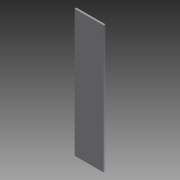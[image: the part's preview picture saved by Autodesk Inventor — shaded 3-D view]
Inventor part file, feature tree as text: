
AUTODESK INVENTOR PART (.ipt)
format: ipt  version: 2011 (Build 150239000, 239)  size: 125,440 bytes
history: native  units: in
note: dims shown in document units (in); Inventor stores cm internally (conversion verified against a paired STEP export)
features: extrude x9, sketch x9
ambient origin geometry x8: Origin, YZ Plane, XZ Plane, XY Plane, X Axis, Y Axis, Z Axis, Center Point
bodies: Solid1 (feature_tree)
feature tree (18):
  extrude  "Extrusion1"  Depth=12.0in
  extrude  "Extrusion2"  Depth=0.5in TaperAngle=0.0deg
  extrude  "Extrusion3"  Depth=1.5in TaperAngle=0.0deg
  extrude  "Extrusion4"  Depth=0.25in TaperAngle=0.0deg
  extrude  "Extrusion5"  Depth=0.5in TaperAngle=0.0deg
  extrude  "Extrusion6"  Depth=1.0in TaperAngle=0.0deg
  extrude  "Extrusion7"  Depth=1.0in TaperAngle=0.0deg
  extrude  "Extrusion8"  [1 undecoded]
  extrude  "Extrusion9"  [1 undecoded]
  sketch  "Sketch1"  dims[d0=5.5in d1=12.0in]
  sketch  "Sketch2"  dims[d2=0.25in d3=0.0in d4=0.5in d5=0.0in]
  sketch  "Sketch3"  dims[d6=0.5in d7=0.0in d8=1.5in d9=0.0in]
  sketch  "Sketch4"  dims[d10=10.0in d11=0.25in d12=0.0in]
  sketch  "Sketch5"  dims[d13=5.0in d14=0.0in d15=0.5in d16=0.0in]
  sketch  "Sketch6"  dims[d17=0.75in d18=1.0in d19=0.0in]
  sketch  "Sketch7"  dims[d20=0.25in d21=1.0in d22=0.0in]
  sketch  "Sketch8"
  sketch  "Sketch9"
note: 2 required parameter values undecoded (feature->parameter linkage not recoverable at this tier; creation-order binding heuristic only, values carry confidence <= 0.55)
